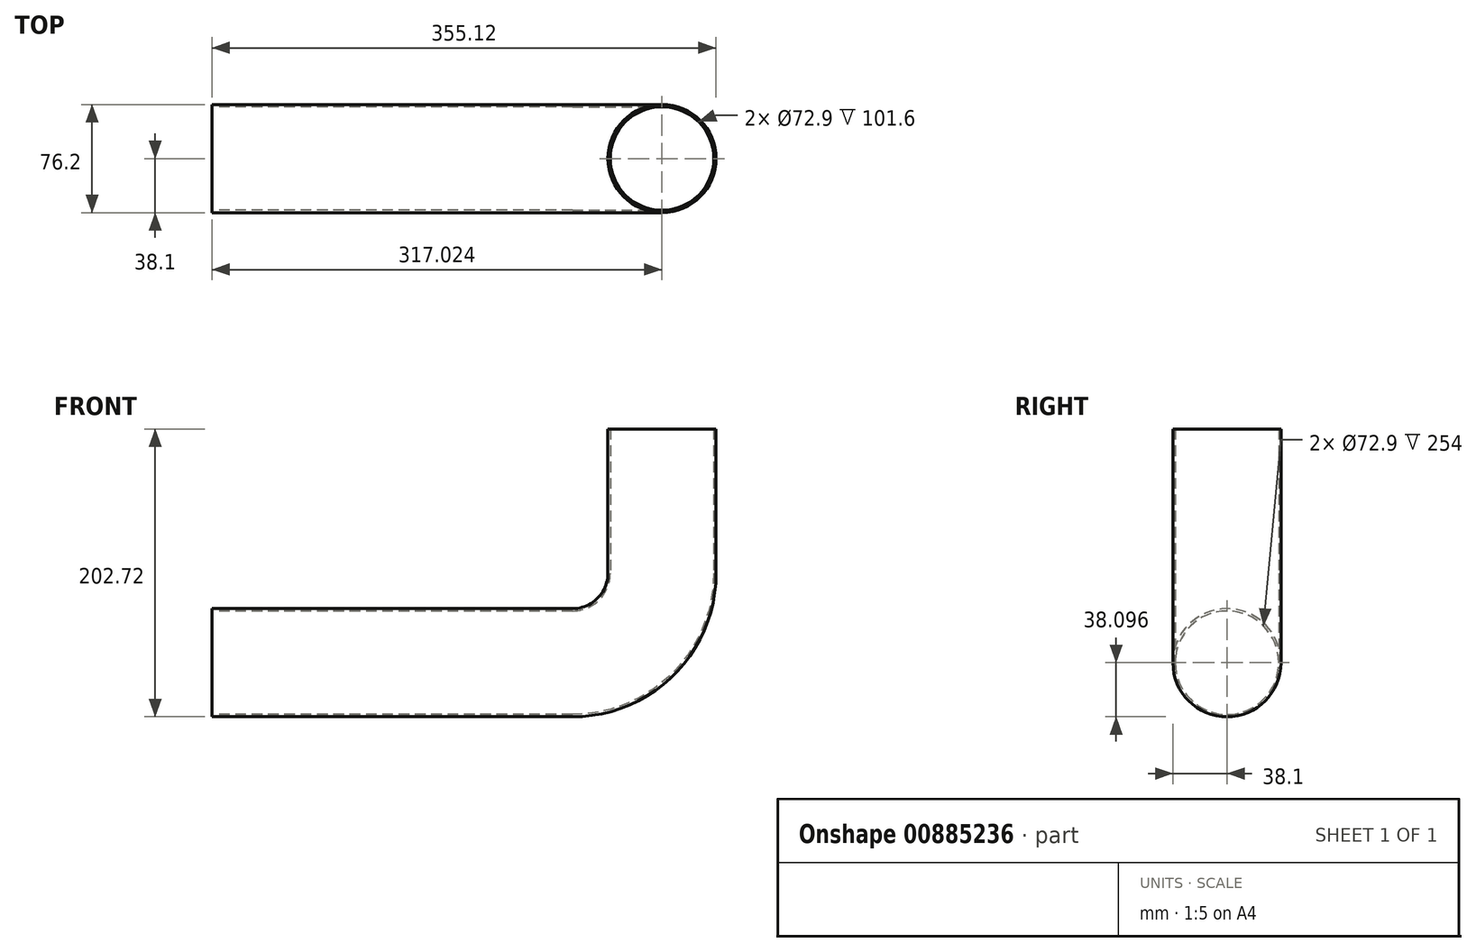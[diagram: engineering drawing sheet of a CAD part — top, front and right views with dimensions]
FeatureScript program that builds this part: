
annotation { "Feature Type Name" : "Feature", "Feature Type Description" : "" }
export const myFeature = defineFeature(function(context is Context, id is Id, definition is map)
    precondition{}
    {
        {
            var Q0;
            Q0=qCreatedBy(makeId("Front.planeOp"),FACE);
            var sketch = newSketch(context, id + "F0", { "sketchPlane" : qUnion([Q0])});
            skArc(sketch, "E0", {"start": v(0, -63.5) * mm, "mid": v(44.9, -44.9) * mm, "end": v(63.5, 0) * mm});
            skLineSegment(sketch, "E1", {"start": v(63.5, 0) * mm, "end": v(63.5, 101.6) * mm});
            skLineSegment(sketch, "E2", {"start": v(0, -63.5) * mm, "end": v(-254, -63.5) * mm});
            skSolve(sketch);
        }
        {
            var Q0;
            Q0=qCreatedBy(makeId("Right.planeOp"),FACE);
            var sketch = newSketch(context, id + "F1", { "sketchPlane" : qUnion([Q0])});
            skCircle(sketch, "E3", {"center": v(0, -63.02) * mm, "radius": 38.1 * mm});
            skCircle(sketch, "E4", {"center": v(0, -63.02) * mm, "radius": 36.45 * mm});
            skSolve(sketch);
        }
        {
            var Q0;
            Q0=makeQuery(id+"F1.imprint","IMPRINT",FACE,{"disambiguationData":[TD([[makeQuery(id+"F1.imprint","IMPRINT",EDGE,{"derivedFrom":sQuery(id+"F1.wireOp",EDGE,"E3")}),1.0]])]});
            var Q1;
            Q1=sQuery(id+"F0.wireOp",EDGE,"E2");
            var Q2;
            Q2=sQuery(id+"F0.wireOp",EDGE,"E0");
            var Q3;
            Q3=sQuery(id+"F0.wireOp",EDGE,"E1");
            sweep(context, id + "F2", {"profiles" : qUnion([Q0]), "path" : qUnion([Q1, Q2, Q3])});
        }
    });
